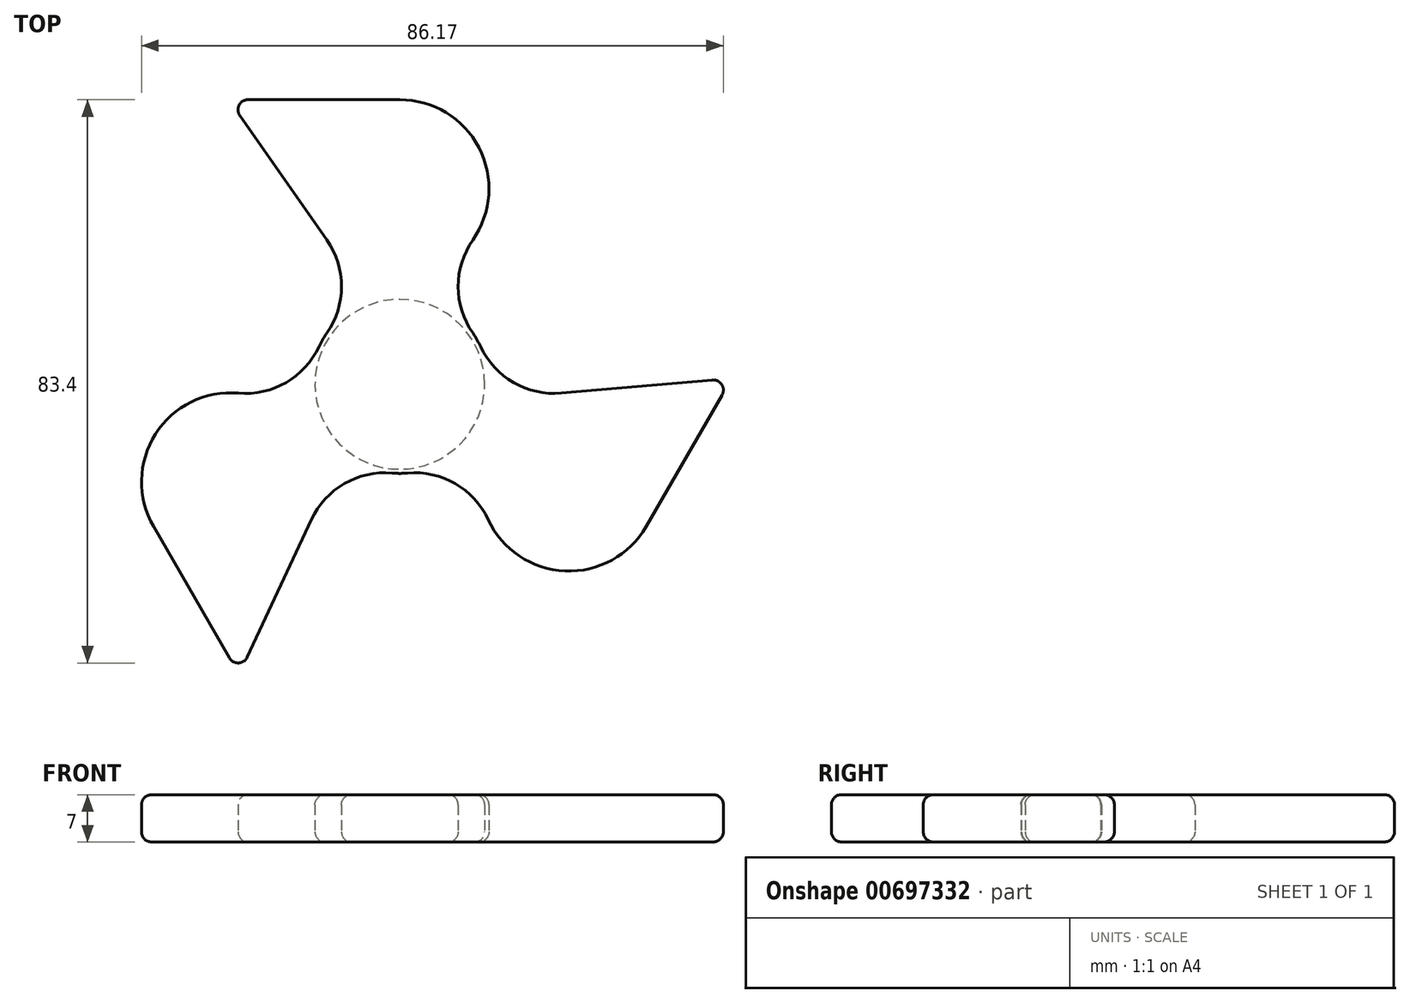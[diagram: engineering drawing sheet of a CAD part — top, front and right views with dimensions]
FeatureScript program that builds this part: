
annotation { "Feature Type Name" : "Feature", "Feature Type Description" : "" }
export const myFeature = defineFeature(function(context is Context, id is Id, definition is map)
    precondition{}
    {
        {
            var Q0;
            Q0=qCreatedBy(makeId("Top.planeOp"),FACE);
            var sketch = newSketch(context, id + "F0", { "sketchPlane" : qUnion([Q0])});
            skCircle(sketch, "E0", {"center": v(0, 0) * mm, "radius": 12.57 * mm});
            skSolve(sketch);
        }
        {
            var Q0;
            Q0=qCreatedBy(makeId("Top.planeOp"),FACE);
            var sketch = newSketch(context, id + "F1", { "sketchPlane" : qUnion([Q0])});
            skCircle(sketch, "E1", {"center": v(0, 0) * mm, "radius": 11.2 * mm});
            skCircle(sketch, "E2", {"center": v(0, 0) * mm, "radius": 13.2 * mm});
            skCircle(sketch, "E3", {"center": v(0, 28.93) * mm, "radius": 11.2 * mm});
            skCircle(sketch, "E4", {"center": v(0, 28.93) * mm, "radius": 13.2 * mm});
            skLineSegment(sketch, "E5", {"start": v(0, 42.13) * mm, "end": v(-25.35, 42.13) * mm});
            skLineSegment(sketch, "E6", {"start": v(-25.35, 42.13) * mm, "end": v(-10.81, 21.36) * mm});
            skCircle(sketch, "E7.1.0", {"center": v(-25.05, -14.46) * mm, "radius": 13.2 * mm});
            skCircle(sketch, "E7.1.1", {"center": v(-25.05, -14.46) * mm, "radius": 11.2 * mm});
            skLineSegment(sketch, "E7.1.2", {"start": v(-23.81, -43.02) * mm, "end": v(-13.1, -20.05) * mm});
            skLineSegment(sketch, "E7.1.3", {"start": v(-36.49, -21.06) * mm, "end": v(-23.81, -43.02) * mm});
            skCircle(sketch, "E7.2.0", {"center": v(25.05, -14.46) * mm, "radius": 13.2 * mm});
            skCircle(sketch, "E7.2.1", {"center": v(25.05, -14.46) * mm, "radius": 11.2 * mm});
            skLineSegment(sketch, "E7.2.2", {"start": v(49.16, 0.89) * mm, "end": v(23.9, -1.31) * mm});
            skLineSegment(sketch, "E7.2.3", {"start": v(36.49, -21.06) * mm, "end": v(49.16, 0.89) * mm});
            skArc(sketch, "E8", {"start": v(-10.81, 7.57) * mm, "mid": v(-8.64, 14.46) * mm, "end": v(-10.81, 21.36) * mm});
            skArc(sketch, "E9.1.0", {"start": v(-1.15, -13.15) * mm, "mid": v(-8.2, -14.72) * mm, "end": v(-13.1, -20.05) * mm});
            skArc(sketch, "E9.2.0", {"start": v(11.96, 5.58) * mm, "mid": v(16.85, 0.25) * mm, "end": v(23.9, -1.31) * mm});
            skArc(sketch, "E10.MirrorCS", {"start": v(10.81, 7.57) * mm, "mid": v(8.64, 14.46) * mm, "end": v(10.81, 21.36) * mm});
            skArc(sketch, "E11.1.0", {"start": v(-11.96, 5.58) * mm, "mid": v(-16.85, 0.25) * mm, "end": v(-23.9, -1.31) * mm});
            skArc(sketch, "E11.2.0", {"start": v(1.15, -13.15) * mm, "mid": v(8.2, -14.72) * mm, "end": v(13.1, -20.05) * mm});
            skSolve(sketch);
        }
        {
            var Q0;
            Q0=makeQuery(id+"F1.imprint","IMPRINT",FACE,{"disambiguationData":[TD([[makeQuery(id+"F1.imprint","IMPRINT",EDGE,{"derivedFrom":sQuery(id+"F1.wireOp",EDGE,"E7.1.1")}),-1.0]])]});
            var Q1;
            {var subQ0=sQuery(id+"F1.wireOp",EDGE,"E7.1.2");Q1=makeQuery(id+"F1.imprint","IMPRINT",FACE,{"disambiguationData":[TD([[makeQuery(id+"F1.imprint","IMPRINT",EDGE,{"derivedFrom":subQ0}),1.0]])]});}
            var Q2;
            Q2=makeQuery(id+"F1.imprint","IMPRINT",FACE,{"disambiguationData":[TD([[makeQuery(id+"F1.imprint","IMPRINT",EDGE,{"derivedFrom":sQuery(id+"F1.wireOp",EDGE,"E7.1.1")}),1.0]])]});
            var Q3;
            Q3=makeQuery(id+"F0.imprint","IMPRINT",FACE,{"disambiguationData":[TD([[makeQuery(id+"F0.imprint","IMPRINT",EDGE,{"derivedFrom":sQuery(id+"F0.wireOp",EDGE,"E0")}),1.0]])]});
            var Q4;
            Q4=makeQuery(id+"F1.imprint","IMPRINT",FACE,{"disambiguationData":[TD([[makeQuery(id+"F1.imprint","IMPRINT",EDGE,{"derivedFrom":sQuery(id+"F1.wireOp",EDGE,"E1")}),-1.0]])]});
            var Q5;
            Q5=makeQuery(id+"F1.imprint","IMPRINT",FACE,{"disambiguationData":[TD([[makeQuery(id+"F1.imprint","IMPRINT",EDGE,{"derivedFrom":sQuery(id+"F1.wireOp",EDGE,"E7.2.1")}),-1.0]])]});
            var Q6;
            Q6=makeQuery(id+"F1.imprint","IMPRINT",FACE,{"disambiguationData":[TD([[makeQuery(id+"F1.imprint","IMPRINT",EDGE,{"derivedFrom":sQuery(id+"F1.wireOp",EDGE,"E3")}),-1.0]])]});
            var Q7;
            {var subQ0=sQuery(id+"F1.wireOp",EDGE,"E9.2.0");Q7=makeQuery(id+"F1.imprint","IMPRINT",FACE,{"disambiguationData":[TD([[makeQuery(id+"F1.imprint","IMPRINT",EDGE,{"derivedFrom":subQ0}),-1.0]])]});}
            var Q8;
            {var subQ0=sQuery(id+"F1.wireOp",EDGE,"E9.1.0");Q8=makeQuery(id+"F1.imprint","IMPRINT",FACE,{"disambiguationData":[TD([[makeQuery(id+"F1.imprint","IMPRINT",EDGE,{"derivedFrom":subQ0}),-1.0]])]});}
            var Q9;
            Q9=makeQuery(id+"F1.imprint","IMPRINT",FACE,{"disambiguationData":[TD([[makeQuery(id+"F1.imprint","IMPRINT",EDGE,{"derivedFrom":sQuery(id+"F1.wireOp",EDGE,"E3")}),1.0]])]});
            var Q10;
            {var subQ0=sQuery(id+"F1.wireOp",EDGE,"E5");Q10=makeQuery(id+"F1.imprint","IMPRINT",FACE,{"disambiguationData":[TD([[makeQuery(id+"F1.imprint","IMPRINT",EDGE,{"derivedFrom":subQ0}),1.0]])]});}
            var Q11;
            {var subQ0=sQuery(id+"F1.wireOp",EDGE,"E8");Q11=makeQuery(id+"F1.imprint","IMPRINT",FACE,{"disambiguationData":[TD([[makeQuery(id+"F1.imprint","IMPRINT",EDGE,{"derivedFrom":subQ0}),-1.0]])]});}
            var Q12;
            Q12=makeQuery(id+"F1.imprint","IMPRINT",FACE,{"disambiguationData":[TD([[makeQuery(id+"F1.imprint","IMPRINT",EDGE,{"derivedFrom":sQuery(id+"F1.wireOp",EDGE,"E7.2.1")}),1.0]])]});
            var Q13;
            {var subQ0=sQuery(id+"F1.wireOp",EDGE,"E7.2.2");Q13=makeQuery(id+"F1.imprint","IMPRINT",FACE,{"disambiguationData":[TD([[makeQuery(id+"F1.imprint","IMPRINT",EDGE,{"derivedFrom":subQ0}),1.0]])]});}
            var Q14;
            Q14=makeQuery(id+"F1.imprint","IMPRINT",FACE,{"disambiguationData":[TD([[makeQuery(id+"F1.imprint","IMPRINT",EDGE,{"derivedFrom":sQuery(id+"F1.wireOp",EDGE,"E1")}),1.0]])]});
            extrude(context, id + "F2", {"entities" : qUnion([Q0, Q1, Q2, Q3, Q4, Q5, Q6, Q7, Q8, Q9, Q10, Q11, Q12, Q13, Q14]), "depth" : 7 * mm, "offsetDistance" : 25 * mm});
        }
        {
            var Q0;
            Q0=makeQuery(id+"F2.opExtrude","CAP_FACE",FACE,{"disambiguationData":[OSD([sQuery(id+"F1.wireOp",EDGE,"E2"),sQuery(id+"F1.wireOp",EDGE,"E4"),sQuery(id+"F1.wireOp",EDGE,"E5"),sQuery(id+"F1.wireOp",EDGE,"E6"),sQuery(id+"F1.wireOp",EDGE,"E7.1.0"),sQuery(id+"F1.wireOp",EDGE,"E7.1.2"),sQuery(id+"F1.wireOp",EDGE,"E7.1.3"),sQuery(id+"F1.wireOp",EDGE,"E7.2.0"),sQuery(id+"F1.wireOp",EDGE,"E7.2.2"),sQuery(id+"F1.wireOp",EDGE,"E7.2.3"),sQuery(id+"F1.wireOp",EDGE,"E8"),sQuery(id+"F1.wireOp",EDGE,"E9.1.0"),sQuery(id+"F1.wireOp",EDGE,"E9.2.0"),sQuery(id+"F1.wireOp",EDGE,"E10.MirrorCS"),sQuery(id+"F1.wireOp",EDGE,"E11.1.0"),sQuery(id+"F1.wireOp",EDGE,"E11.2.0")])],"isStart":false});
            var Q1;
            Q1=makeQuery(id+"F2.opExtrude","CAP_EDGE",EDGE,{"disambiguationData":[OSD([sQuery(id+"F1.wireOp",EDGE,"E7.1.2")])],"isStart":true});
            var Q2;
            Q2=makeQuery(id+"F2.opExtrude","CAP_EDGE",EDGE,{"disambiguationData":[OSD([sQuery(id+"F1.wireOp",EDGE,"E9.1.0")])],"isStart":true});
            var Q3;
            Q3=makeQuery(id+"F2.opExtrude","CAP_EDGE",EDGE,{"disambiguationData":[OSD([sQuery(id+"F1.wireOp",EDGE,"E11.2.0")])],"isStart":true});
            var Q4;
            Q4=makeQuery(id+"F2.opExtrude","SWEPT_EDGE",EDGE,{"disambiguationData":[OSD([sQuery(id+"F1.wireOp",EDGE,"E2"),sQuery(id+"F1.wireOp",EDGE,"E11.2.0")])]});
            var Q5;
            {var subQ0=sQuery(id+"F1.wireOp",EDGE,"E2");Q5=makeQuery(id+"F2.opExtrude","CAP_EDGE",EDGE,{"disambiguationData":[OSD([subQ0]),TDD([makeQuery(id+"F1.imprint","IMPRINT",EDGE,{"disambiguationData":[TD([[makeQuery(id+"F1.imprint","INTERSECT",VERTEX,{"derivedFrom":[subQ0,sQuery(id+"F1.wireOp",EDGE,"E9.1.0")]}),-1.0]])],"derivedFrom":subQ0})])],"isStart":true});}
            var Q6;
            Q6=makeQuery(id+"F2.opExtrude","CAP_EDGE",EDGE,{"disambiguationData":[OSD([sQuery(id+"F1.wireOp",EDGE,"E7.2.0")])],"isStart":true});
            var Q7;
            Q7=makeQuery(id+"F2.opExtrude","SWEPT_EDGE",EDGE,{"disambiguationData":[OSD([sQuery(id+"F1.wireOp",EDGE,"E7.2.0"),sQuery(id+"F1.wireOp",EDGE,"E7.2.3")])]});
            var Q8;
            Q8=makeQuery(id+"F2.opExtrude","CAP_EDGE",EDGE,{"disambiguationData":[OSD([sQuery(id+"F1.wireOp",EDGE,"E7.2.3")])],"isStart":true});
            var Q9;
            Q9=makeQuery(id+"F2.opExtrude","SWEPT_EDGE",EDGE,{"disambiguationData":[OSD([sQuery(id+"F1.wireOp",EDGE,"E7.2.2"),sQuery(id+"F1.wireOp",EDGE,"E7.2.3")])]});
            var Q10;
            Q10=makeQuery(id+"F2.opExtrude","SWEPT_EDGE",EDGE,{"disambiguationData":[OSD([sQuery(id+"F1.wireOp",EDGE,"E7.1.2"),sQuery(id+"F1.wireOp",EDGE,"E7.1.3")])]});
            var Q11;
            Q11=makeQuery(id+"F2.opExtrude","SWEPT_EDGE",EDGE,{"disambiguationData":[OSD([sQuery(id+"F1.wireOp",EDGE,"E7.1.0"),sQuery(id+"F1.wireOp",EDGE,"E7.1.2"),sQuery(id+"F1.wireOp",EDGE,"E9.1.0")])]});
            var Q12;
            Q12=makeQuery(id+"F2.opExtrude","CAP_FACE",FACE,{"disambiguationData":[OSD([sQuery(id+"F0.wireOp",EDGE,"E0")])],"isStart":false});
            var Q13;
            Q13=makeQuery(id+"F2.opExtrude","SWEPT_FACE",FACE,{"disambiguationData":[OSD([sQuery(id+"F1.wireOp",EDGE,"E10.MirrorCS")])]});
            var Q14;
            Q14=makeQuery(id+"F2.opExtrude","CAP_EDGE",EDGE,{"disambiguationData":[OSD([sQuery(id+"F1.wireOp",EDGE,"E4")])],"isStart":true});
            var Q15;
            Q15=makeQuery(id+"F2.opExtrude","CAP_EDGE",EDGE,{"disambiguationData":[OSD([sQuery(id+"F1.wireOp",EDGE,"E4")])],"isStart":false});
            var Q16;
            Q16=makeQuery(id+"F2.opExtrude","CAP_EDGE",EDGE,{"disambiguationData":[OSD([sQuery(id+"F1.wireOp",EDGE,"E5")])],"isStart":false});
            var Q17;
            Q17=makeQuery(id+"F2.opExtrude","CAP_EDGE",EDGE,{"disambiguationData":[OSD([sQuery(id+"F1.wireOp",EDGE,"E8")])],"isStart":false});
            var Q18;
            Q18=makeQuery(id+"F2.opExtrude","CAP_EDGE",EDGE,{"disambiguationData":[OSD([sQuery(id+"F1.wireOp",EDGE,"E6")])],"isStart":false});
            var Q19;
            Q19=makeQuery(id+"F2.opExtrude","CAP_EDGE",EDGE,{"disambiguationData":[OSD([sQuery(id+"F1.wireOp",EDGE,"E11.1.0")])],"isStart":false});
            var Q20;
            Q20=makeQuery(id+"F2.opExtrude","CAP_EDGE",EDGE,{"disambiguationData":[OSD([sQuery(id+"F1.wireOp",EDGE,"E7.1.0")])],"isStart":false});
            var Q21;
            Q21=makeQuery(id+"F2.opExtrude","CAP_EDGE",EDGE,{"disambiguationData":[OSD([sQuery(id+"F1.wireOp",EDGE,"E7.1.3")])],"isStart":false});
            var Q22;
            Q22=makeQuery(id+"F2.opExtrude","CAP_EDGE",EDGE,{"disambiguationData":[OSD([sQuery(id+"F1.wireOp",EDGE,"E7.2.2")])],"isStart":false});
            var Q23;
            Q23=makeQuery(id+"F2.opExtrude","CAP_EDGE",EDGE,{"disambiguationData":[OSD([sQuery(id+"F1.wireOp",EDGE,"E9.2.0")])],"isStart":false});
            var Q24;
            Q24=makeQuery(id+"F2.opExtrude","SWEPT_EDGE",EDGE,{"disambiguationData":[OSD([sQuery(id+"F1.wireOp",EDGE,"E7.2.0"),sQuery(id+"F1.wireOp",EDGE,"E7.2.2"),sQuery(id+"F1.wireOp",EDGE,"E9.2.0")])]});
            var Q25;
            Q25=makeQuery(id+"F2.opExtrude","SWEPT_FACE",FACE,{"disambiguationData":[OSD([sQuery(id+"F1.wireOp",EDGE,"E4")])]});
            var Q26;
            Q26=makeQuery(id+"F2.opExtrude","CAP_EDGE",EDGE,{"disambiguationData":[OSD([sQuery(id+"F1.wireOp",EDGE,"E7.1.0")])],"isStart":true});
            var Q27;
            Q27=makeQuery(id+"F2.opExtrude","SWEPT_FACE",FACE,{"disambiguationData":[OSD([sQuery(id+"F1.wireOp",EDGE,"E7.1.0")])]});
            var Q28;
            Q28=makeQuery(id+"F2.opExtrude","CAP_EDGE",EDGE,{"disambiguationData":[OSD([sQuery(id+"F1.wireOp",EDGE,"E9.2.0")])],"isStart":true});
            var Q29;
            Q29=makeQuery(id+"F2.opExtrude","SWEPT_EDGE",EDGE,{"disambiguationData":[OSD([sQuery(id+"F1.wireOp",EDGE,"E5"),sQuery(id+"F1.wireOp",EDGE,"E6")])]});
            var Q30;
            Q30=makeQuery(id+"F2.opExtrude","CAP_EDGE",EDGE,{"disambiguationData":[OSD([sQuery(id+"F0.wireOp",EDGE,"E0")])],"isStart":false});
            var Q31;
            Q31=makeQuery(id+"F2.opExtrude","CAP_EDGE",EDGE,{"disambiguationData":[OSD([sQuery(id+"F1.wireOp",EDGE,"E6")])],"isStart":true});
            var Q32;
            Q32=makeQuery(id+"F2.opExtrude","SWEPT_EDGE",EDGE,{"disambiguationData":[OSD([sQuery(id+"F1.wireOp",EDGE,"E7.1.0"),sQuery(id+"F1.wireOp",EDGE,"E7.1.3")])]});
            var Q33;
            Q33=makeQuery(id+"F2.opExtrude","SWEPT_EDGE",EDGE,{"disambiguationData":[OSD([sQuery(id+"F1.wireOp",EDGE,"E4"),sQuery(id+"F1.wireOp",EDGE,"E5")])]});
            var Q34;
            Q34=makeQuery(id+"F2.opExtrude","CAP_EDGE",EDGE,{"disambiguationData":[OSD([sQuery(id+"F1.wireOp",EDGE,"E7.2.2")])],"isStart":true});
            var Q35;
            Q35=makeQuery(id+"F2.opExtrude","CAP_EDGE",EDGE,{"disambiguationData":[OSD([sQuery(id+"F1.wireOp",EDGE,"E5")])],"isStart":true});
            var Q36;
            Q36=makeQuery(id+"F2.opExtrude","CAP_EDGE",EDGE,{"disambiguationData":[OSD([sQuery(id+"F1.wireOp",EDGE,"E9.1.0")])],"isStart":false});
            var Q37;
            Q37=makeQuery(id+"F2.opExtrude","SWEPT_EDGE",EDGE,{"disambiguationData":[OSD([sQuery(id+"F1.wireOp",EDGE,"E2"),sQuery(id+"F1.wireOp",EDGE,"E11.1.0")])]});
            var Q38;
            Q38=makeQuery(id+"F2.opExtrude","SWEPT_EDGE",EDGE,{"disambiguationData":[OSD([sQuery(id+"F1.wireOp",EDGE,"E7.1.0"),sQuery(id+"F1.wireOp",EDGE,"E11.1.0")])]});
            var Q39;
            Q39=makeQuery(id+"F2.opExtrude","SWEPT_EDGE",EDGE,{"disambiguationData":[OSD([sQuery(id+"F1.wireOp",EDGE,"E2"),sQuery(id+"F1.wireOp",EDGE,"E9.2.0")])]});
            var Q40;
            Q40=makeQuery(id+"F2.opExtrude","CAP_EDGE",EDGE,{"disambiguationData":[OSD([sQuery(id+"F1.wireOp",EDGE,"E10.MirrorCS")])],"isStart":true});
            var Q41;
            Q41=makeQuery(id+"F2.opExtrude","SWEPT_EDGE",EDGE,{"disambiguationData":[OSD([sQuery(id+"F1.wireOp",EDGE,"E4"),sQuery(id+"F1.wireOp",EDGE,"E10.MirrorCS")])]});
            var Q42;
            Q42=makeQuery(id+"F2.opExtrude","SWEPT_EDGE",EDGE,{"disambiguationData":[OSD([sQuery(id+"F1.wireOp",EDGE,"E4"),sQuery(id+"F1.wireOp",EDGE,"E6"),sQuery(id+"F1.wireOp",EDGE,"E8")])]});
            var Q43;
            Q43=makeQuery(id+"F2.opExtrude","SWEPT_EDGE",EDGE,{"disambiguationData":[OSD([sQuery(id+"F1.wireOp",EDGE,"E7.2.0"),sQuery(id+"F1.wireOp",EDGE,"E11.2.0")])]});
            var Q44;
            Q44=makeQuery(id+"F2.opExtrude","CAP_EDGE",EDGE,{"disambiguationData":[OSD([sQuery(id+"F1.wireOp",EDGE,"E10.MirrorCS")])],"isStart":false});
            var Q45;
            {var subQ0=sQuery(id+"F1.wireOp",EDGE,"E2");Q45=makeQuery(id+"F2.opExtrude","CAP_EDGE",EDGE,{"disambiguationData":[OSD([subQ0]),TDD([makeQuery(id+"F1.imprint","IMPRINT",EDGE,{"disambiguationData":[TD([[makeQuery(id+"F1.imprint","INTERSECT",VERTEX,{"derivedFrom":[subQ0,sQuery(id+"F1.wireOp",EDGE,"E9.2.0")]}),-1.0]])],"derivedFrom":subQ0})])],"isStart":true});}
            var Q46;
            Q46=makeQuery(id+"F2.opExtrude","CAP_EDGE",EDGE,{"disambiguationData":[OSD([sQuery(id+"F1.wireOp",EDGE,"E7.1.3")])],"isStart":true});
            var Q47;
            Q47=makeQuery(id+"F2.opExtrude","CAP_EDGE",EDGE,{"disambiguationData":[OSD([sQuery(id+"F1.wireOp",EDGE,"E11.1.0")])],"isStart":true});
            var Q48;
            {var subQ0=sQuery(id+"F1.wireOp",EDGE,"E2");Q48=makeQuery(id+"F2.opExtrude","CAP_EDGE",EDGE,{"disambiguationData":[OSD([subQ0]),TDD([makeQuery(id+"F1.imprint","IMPRINT",EDGE,{"disambiguationData":[TD([[makeQuery(id+"F1.imprint","INTERSECT",VERTEX,{"derivedFrom":[subQ0,sQuery(id+"F1.wireOp",EDGE,"E9.2.0")]}),-1.0]])],"derivedFrom":subQ0})])],"isStart":false});}
            var Q49;
            {var subQ0=sQuery(id+"F1.wireOp",EDGE,"E2");Q49=makeQuery(id+"F2.opExtrude","CAP_EDGE",EDGE,{"disambiguationData":[OSD([subQ0]),TDD([makeQuery(id+"F1.imprint","IMPRINT",EDGE,{"disambiguationData":[TD([[makeQuery(id+"F1.imprint","INTERSECT",VERTEX,{"derivedFrom":[subQ0,sQuery(id+"F1.wireOp",EDGE,"E8")]}),-1.0]])],"derivedFrom":subQ0})])],"isStart":true});}
            var Q50;
            Q50=makeQuery(id+"F2.opExtrude","CAP_EDGE",EDGE,{"disambiguationData":[OSD([sQuery(id+"F1.wireOp",EDGE,"E7.2.0")])],"isStart":false});
            var Q51;
            Q51=makeQuery(id+"F2.opExtrude","CAP_EDGE",EDGE,{"disambiguationData":[OSD([sQuery(id+"F1.wireOp",EDGE,"E11.2.0")])],"isStart":false});
            var Q52;
            {var subQ0=sQuery(id+"F1.wireOp",EDGE,"E2");Q52=makeQuery(id+"F2.opExtrude","CAP_EDGE",EDGE,{"disambiguationData":[OSD([subQ0]),TDD([makeQuery(id+"F1.imprint","IMPRINT",EDGE,{"disambiguationData":[TD([[makeQuery(id+"F1.imprint","INTERSECT",VERTEX,{"derivedFrom":[subQ0,sQuery(id+"F1.wireOp",EDGE,"E9.1.0")]}),-1.0]])],"derivedFrom":subQ0})])],"isStart":false});}
            var Q53;
            Q53=makeQuery(id+"F2.opExtrude","CAP_EDGE",EDGE,{"disambiguationData":[OSD([sQuery(id+"F1.wireOp",EDGE,"E7.2.3")])],"isStart":false});
            var Q54;
            Q54=makeQuery(id+"F2.opExtrude","CAP_EDGE",EDGE,{"disambiguationData":[OSD([sQuery(id+"F1.wireOp",EDGE,"E8")])],"isStart":true});
            var Q55;
            Q55=makeQuery(id+"F2.opExtrude","CAP_EDGE",EDGE,{"disambiguationData":[OSD([sQuery(id+"F0.wireOp",EDGE,"E0")])],"isStart":true});
            var Q56;
            Q56=makeQuery(id+"F2.opExtrude","SWEPT_EDGE",EDGE,{"disambiguationData":[OSD([sQuery(id+"F1.wireOp",EDGE,"E2"),sQuery(id+"F1.wireOp",EDGE,"E9.1.0")])]});
            var Q57;
            Q57=makeQuery(id+"F2.opExtrude","SWEPT_EDGE",EDGE,{"disambiguationData":[OSD([sQuery(id+"F1.wireOp",EDGE,"E2"),sQuery(id+"F1.wireOp",EDGE,"E10.MirrorCS")])]});
            var Q58;
            Q58=makeQuery(id+"F2.opExtrude","SWEPT_EDGE",EDGE,{"disambiguationData":[OSD([sQuery(id+"F1.wireOp",EDGE,"E2"),sQuery(id+"F1.wireOp",EDGE,"E8")])]});
            var Q59;
            {var subQ0=sQuery(id+"F1.wireOp",EDGE,"E2");Q59=makeQuery(id+"F2.opExtrude","CAP_EDGE",EDGE,{"disambiguationData":[OSD([subQ0]),TDD([makeQuery(id+"F1.imprint","IMPRINT",EDGE,{"disambiguationData":[TD([[makeQuery(id+"F1.imprint","INTERSECT",VERTEX,{"derivedFrom":[subQ0,sQuery(id+"F1.wireOp",EDGE,"E8")]}),-1.0]])],"derivedFrom":subQ0})])],"isStart":false});}
            var Q60;
            Q60=makeQuery(id+"F2.opExtrude","CAP_EDGE",EDGE,{"disambiguationData":[OSD([sQuery(id+"F1.wireOp",EDGE,"E7.1.2")])],"isStart":false});
            fillet(context, id + "F3", {"entities" : qUnion([Q0, Q1, Q2, Q3, Q4, Q5, Q6, Q7, Q8, Q9, Q10, Q11, Q12, Q13, Q14, Q15, Q16, Q17, Q18, Q19, Q20, Q21, Q22, Q23, Q24, Q25, Q26, Q27, Q28, Q29, Q30, Q31, Q32, Q33, Q34, Q35, Q36, Q37, Q38, Q39, Q40, Q41, Q42, Q43, Q44, Q45, Q46, Q47, Q48, Q49, Q50, Q51, Q52, Q53, Q54, Q55, Q56, Q57, Q58, Q59, Q60]), "radius" : 1.5 * mm, "tangentPropagation" : true, "allowEdgeOverflow" : false});
        }
    });
